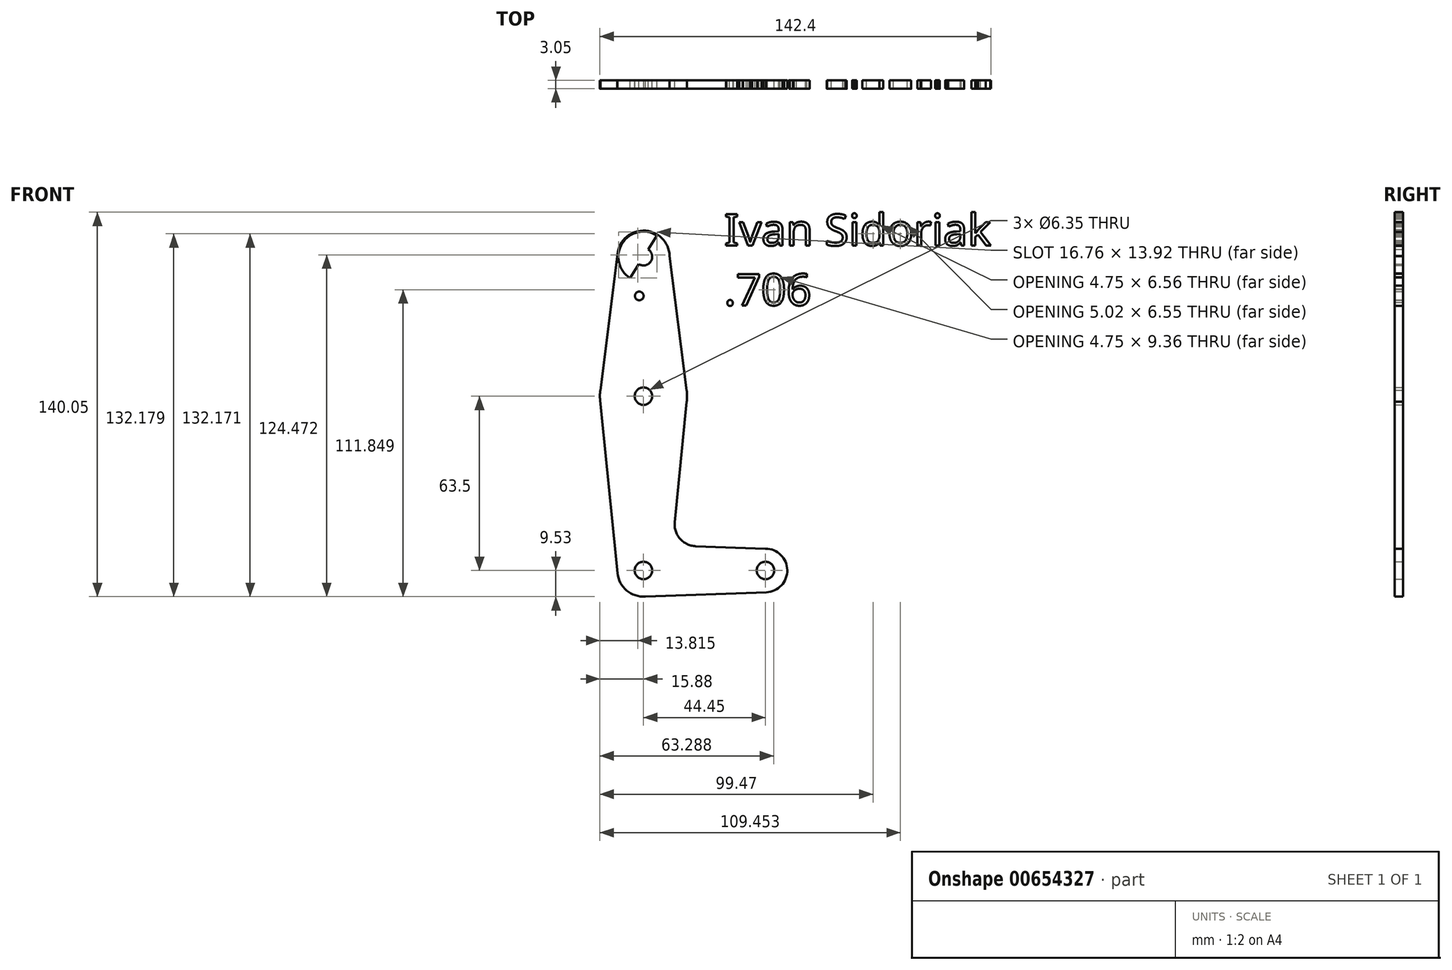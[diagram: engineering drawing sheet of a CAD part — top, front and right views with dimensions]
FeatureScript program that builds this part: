
annotation { "Feature Type Name" : "Feature", "Feature Type Description" : "" }
export const myFeature = defineFeature(function(context is Context, id is Id, definition is map)
    precondition{}
    {
        {
            var Q0;
            Q0=qCreatedBy(makeId("Front.planeOp"),FACE);
            var sketch = newSketch(context, id + "F0", { "sketchPlane" : qUnion([Q0])});
            skLineSegment(sketch, "E0", {"start": v(0, 114.3) * mm, "end": v(0, 0) * mm});
            skLineSegment(sketch, "E1", {"start": v(0, 0) * mm, "end": v(44.45, 0) * mm});
            skCircle(sketch, "E2", {"center": v(0, 114.3) * mm, "radius": 9.16 * mm});
            skCircle(sketch, "E3", {"center": v(0, 63.5) * mm, "radius": 15.88 * mm});
            skCircle(sketch, "E4", {"center": v(0, 0) * mm, "radius": 9.53 * mm});
            skCircle(sketch, "E5", {"center": v(44.45, 0) * mm, "radius": 7.94 * mm});
            skCircle(sketch, "E6", {"center": v(0, 114.3) * mm, "radius": 9.53 * mm});
            skPoint(sketch, "E7.end.orphan", {"position": v(-15.72, 65.68) * mm});
            skPoint(sketch, "E8.end.orphan", {"position": v(15.75, 65.5) * mm});
            skPoint(sketch, "E9.orphan", {"position": v(15.75, 61.5) * mm});
            skLineSegment(sketch, "E10", {"start": v(-9.52, 114.32) * mm, "end": v(-15.72, 65.68) * mm});
            skLineSegment(sketch, "E11", {"start": v(4.9, 122.04) * mm, "end": v(-5.09, 106.25) * mm});
            skLineSegment(sketch, "E12", {"start": v(9.52, 114.6) * mm, "end": v(15.75, 65.5) * mm});
            skPoint(sketch, "E13.end.orphan", {"position": v(44.45, -17.73) * mm});
            skPoint(sketch, "E13.start.orphan", {"position": v(0, -9.53) * mm});
            skLineSegment(sketch, "E14", {"start": v(19.01, 8.85) * mm, "end": v(44.45, 7.94) * mm});
            skLineSegment(sketch, "E15", {"start": v(0, -9.53) * mm, "end": v(0.68, -9.5) * mm});
            skCircle(sketch, "E16", {"center": v(-1.54, 100.03) * mm, "radius": 1.59 * mm});
            skCircle(sketch, "E17", {"center": v(0, 114.3) * mm, "radius": 3.18 * mm});
            skCircle(sketch, "E18", {"center": v(0, 63.5) * mm, "radius": 3.18 * mm});
            skLineSegment(sketch, "E19", {"start": v(15.75, 61.5) * mm, "end": v(11.38, 17.58) * mm});
            skPoint(sketch, "E20.end.orphan", {"position": v(9.64, 30.6) * mm});
            skPoint(sketch, "E21", {"position": v(-12.62, 30.6) * mm});
            skCircle(sketch, "E22", {"center": v(0, 0) * mm, "radius": 3.18 * mm});
            skCircle(sketch, "E23", {"center": v(44.45, 0) * mm, "radius": 3.18 * mm});
            skPoint(sketch, "E24.newPointB", {"position": v(9.64, 0) * mm});
            skArc(sketch, "E24.filletArc", {"start": v(11.38, 17.58) * mm, "mid": v(13.3, 11.56) * mm, "end": v(19.01, 8.85) * mm});
            skPoint(sketch, "E25.orphan", {"position": v(-15.72, 61.21) * mm});
            skPoint(sketch, "E26.start.orphan", {"position": v(-9.53, 0) * mm});
            skLineSegment(sketch, "E27", {"start": v(-9.53, 0) * mm, "end": v(-9.33, -1.9) * mm});
            skLineSegment(sketch, "E28", {"start": v(0.68, -9.5) * mm, "end": v(0, -9.53) * mm});
            skLineSegment(sketch, "E29", {"start": v(0, -9.53) * mm, "end": v(44.73, -7.93) * mm});
            skLineSegment(sketch, "E30", {"start": v(-15.8, 61.91) * mm, "end": v(-9.48, -0.95) * mm});
            skText(sketch, "E31", { "text": "Ivan Sidoriak \n.706", "fontName": "NotoSans-Regular.ttf"});
            const initialGuessF0  = {"E31": [0.0294, 0.11836, 1, 0, 0.01152]};
            skSetInitialGuess(sketch, initialGuessF0);
            skSolve(sketch);
        }
        {
            var Q0;
            Q0=qCreatedBy(makeId("Front.planeOp"),FACE);
            var sketch = newSketch(context, id + "F1", { "sketchPlane" : qUnion([Q0])});
            skSolve(sketch);
        }
        {
            var Q0;
            Q0 = qSketchRegion(id + "F0", true);
            extrude(context, id + "F2", {"entities" : qUnion([Q0]), "depth" : 3.05 * mm, "offsetDistance" : 25.4 * mm});
        }
        {
            var Q0;
            Q0 = qSketchRegion(id + "F0", true);
            var Q1;
            {var subQ0=sQuery(id+"F0.wireOp",EDGE,"E17");var subQ1=sQuery(id+"F0.wireOp",EDGE,"E0");var subQ2=makeQuery(id+"F0.imprint","INTERSECT",VERTEX,{"derivedFrom":[subQ1,subQ0]});Q1=makeQuery(id+"F0.imprint","IMPRINT",FACE,{"disambiguationData":[TD([[makeQuery(id+"F0.imprint","IMPRINT",EDGE,{"disambiguationData":[TD([[subQ2,-1.0]])],"derivedFrom":subQ1}),1.0]])]});}
            var Q2;
            {var subQ0=sQuery(id+"F0.wireOp",EDGE,"E11");var subQ1=sQuery(id+"F0.wireOp",EDGE,"E2");var subQ2=makeQuery(id+"F0.imprint","INTERSECT",VERTEX,{"disambiguationData":[OD(0.0)],"derivedFrom":[subQ1,subQ0]});Q2=makeQuery(id+"F0.imprint","IMPRINT",FACE,{"disambiguationData":[TD([[makeQuery(id+"F0.imprint","IMPRINT",EDGE,{"disambiguationData":[TD([[subQ2,1.0]])],"derivedFrom":subQ1}),-1.0]])]});}
            var Q3;
            {var subQ0=sQuery(id+"F0.wireOp",EDGE,"E17");var subQ1=sQuery(id+"F0.wireOp",EDGE,"E0");var subQ2=makeQuery(id+"F0.imprint","INTERSECT",VERTEX,{"derivedFrom":[subQ1,subQ0]});Q3=makeQuery(id+"F0.imprint","IMPRINT",FACE,{"disambiguationData":[TD([[makeQuery(id+"F0.imprint","IMPRINT",EDGE,{"disambiguationData":[TD([[subQ2,-1.0]])],"derivedFrom":subQ1}),-1.0]])]});}
            var Q4;
            {var subQ0=sQuery(id+"F0.wireOp",EDGE,"E2");var subQ1=sQuery(id+"F0.wireOp",EDGE,"E0");var subQ2=makeQuery(id+"F0.imprint","INTERSECT",VERTEX,{"derivedFrom":[subQ1,subQ0]});Q4=makeQuery(id+"F0.imprint","IMPRINT",FACE,{"disambiguationData":[TD([[makeQuery(id+"F0.imprint","IMPRINT",EDGE,{"disambiguationData":[TD([[subQ2,-1.0]])],"derivedFrom":subQ1}),-1.0]])]});}
            var Q5;
            {var subQ0=sQuery(id+"F0.wireOp",EDGE,"E4");var subQ1=sQuery(id+"F0.wireOp",EDGE,"E0");var subQ2=makeQuery(id+"F0.imprint","INTERSECT",VERTEX,{"derivedFrom":[subQ1,subQ0]});Q5=makeQuery(id+"F0.imprint","IMPRINT",FACE,{"disambiguationData":[TD([[makeQuery(id+"F0.imprint","IMPRINT",EDGE,{"disambiguationData":[TD([[subQ2,-1.0]])],"derivedFrom":subQ1}),1.0]])]});}
            extrude(context, id + "F3", {"entities" : qUnion([Q0, Q1, Q2, Q3, Q4, Q5]), "operationType" : NewBodyOperationType.ADD, "depth" : 3.05 * mm, "offsetDistance" : 25.4 * mm});
        }
    });
